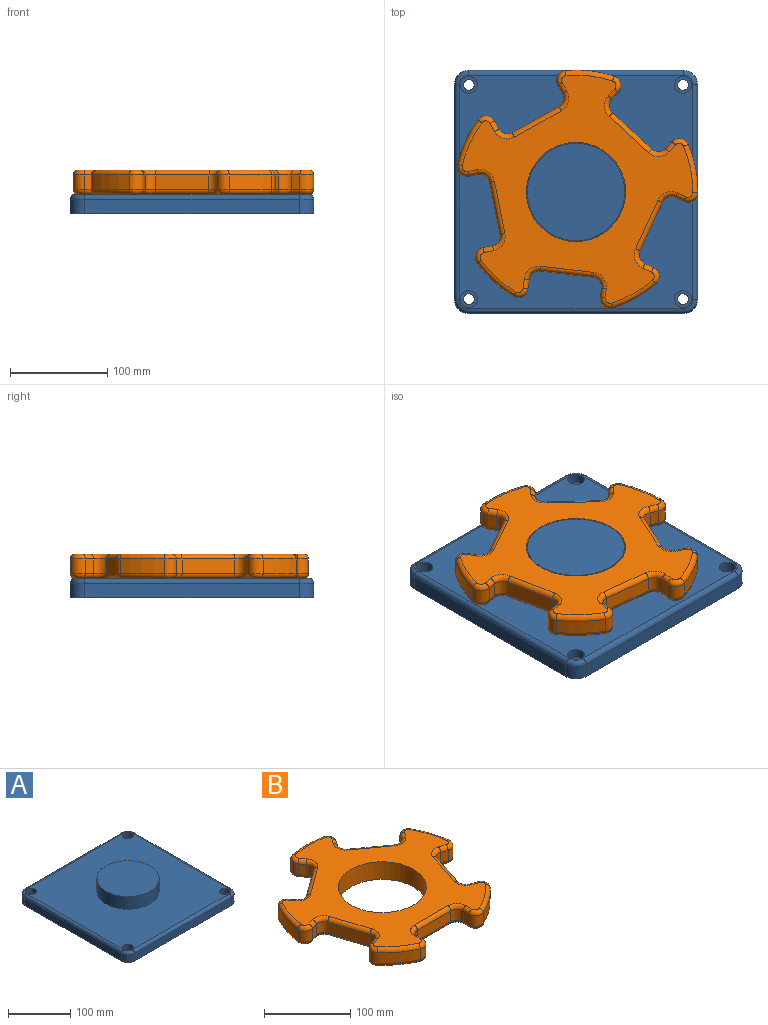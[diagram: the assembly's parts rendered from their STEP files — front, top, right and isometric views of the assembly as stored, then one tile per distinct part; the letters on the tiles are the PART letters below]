
ASSEMBLY  parts=2 mates=1
PART A: 32 faces, bbox 252.5x252.5x45 mm
  f0: plane 220x15mm, normal (1,0,0), area 3300mm2, adj f5,f8,f11,f27
  f1: plane 220x15mm, normal (0,1,0), area 3300mm2, adj f5,f8,f9,f31
  f2: plane 220x15mm, normal (-1,0,0), area 3300mm2, adj f5,f9,f10,f28
  f3: plane 220x15mm, normal (0,-1,0), area 3300mm2, adj f5,f10,f11,f24
  f4: plane 240x240mm, normal (0,0,1), area 48725.4mm2, adj f6,f14,f17,f20,f23,f24,f25,f26
  f5: plane 250x250mm, normal (0,0,-1), area 61926.7mm2, adj f0,f1,f2,f3,f8,f9,f10,f11
  f6: cylinder r=50mm len=100mm, axis (0,0,-1), area 7854mm2, adj f4,f7
  f7: plane 100x100mm, normal (0,0,1), area 7854mm2, adj f6
  f8: cylinder r=15mm len=15mm, axis (0,0,-1), area 353.4mm2, adj f0,f1,f5,f29
  f9: cylinder r=15mm len=15mm, axis (0,0,1), area 353.4mm2, adj f1,f2,f5,f30
  f10: cylinder r=15mm len=15mm, axis (0,0,-1), area 353.4mm2, adj f2,f3,f5,f26
  f11: cylinder r=15mm len=15mm, axis (0,0,1), area 353.4mm2, adj f0,f3,f5,f25
  f12: cylinder r=5.5mm len=11mm, axis (0,0,1), area 345.6mm2, adj f5,f13
  f13: plane 17.25x17.25mm, normal (0,0,1), area 138.7mm2, adj f12,f14
  f14: cylinder r=8.62mm len=17.25mm, axis (0,0,1), area 541.9mm2, adj f4,f13
  f15: cylinder r=5.5mm len=11mm, axis (0,0,1), area 345.6mm2, adj f5,f16
  f16: plane 17.25x17.25mm, normal (0,0,1), area 138.7mm2, adj f15,f17
  f17: cylinder r=8.62mm len=17.25mm, axis (0,0,1), area 541.9mm2, adj f4,f16
  f18: cylinder r=5.5mm len=11mm, axis (0,0,1), area 345.6mm2, adj f5,f19
  f19: plane 17.25x17.25mm, normal (0,0,1), area 138.7mm2, adj f18,f20
  f20: cylinder r=8.62mm len=17.25mm, axis (0,0,1), area 541.9mm2, adj f4,f19
  f21: cylinder r=5.5mm len=11mm, axis (0,0,1), area 345.6mm2, adj f5,f22
  f22: plane 17.25x17.25mm, normal (0,0,1), area 138.7mm2, adj f21,f23
  f23: cylinder r=8.62mm len=17.25mm, axis (0,0,1), area 541.9mm2, adj f4,f22
  f24: cylinder r=5mm len=220mm, axis (-1,0,0), area 1727.9mm2, adj f3,f4,f25,f26
  f25: torus R=10mm, axis (0,0,1), area 162.6mm2, adj f4,f11,f24,f27
  f26: torus R=10mm, axis (0,0,1), area 162.6mm2, adj f4,f10,f24,f28
  f27: cylinder r=5mm len=220mm, axis (0,-1,0), area 1727.9mm2, adj f0,f4,f25,f29
  f28: cylinder r=5mm len=220mm, axis (0,1,0), area 1727.9mm2, adj f2,f4,f26,f30
  f29: torus R=10mm, axis (0,0,1), area 162.6mm2, adj f4,f8,f27,f31
  f30: torus R=10mm, axis (0,0,1), area 162.6mm2, adj f4,f9,f28,f31
  f31: cylinder r=5mm len=220mm, axis (1,0,0), area 1727.9mm2, adj f1,f4,f29,f30
PART B: 123 faces, bbox 268.9x258.5x25 mm
  f0: plane 238.57x229.73mm, normal (0,0,1), area 21505.7mm2, adj f6,f83,f84,f85,f86,f87,f88,f89
  f1: plane 238.57x229.73mm, normal (0,0,-1), area 21505.7mm2, adj f6,f43,f44,f45,f46,f47,f48,f49
  f2: cylinder r=125mm len=47.82mm, axis (0,0,-1), area 759.5mm2, adj f34,f42,f74,f114
  f3: cylinder r=125mm len=50.29mm, axis (0,0,-1), area 759.5mm2, adj f27,f35,f75,f115
  f4: cylinder r=125mm len=47.82mm, axis (0,0,-1), area 759.5mm2, adj f20,f28,f59,f99
  f5: cylinder r=125mm len=40.68mm, axis (0,0,-1), area 759.5mm2, adj f13,f21,f43,f83
  f6: cylinder r=51mm len=102mm, axis (0,0,-1), area 8011.1mm2, adj f0,f1
  f7: cylinder r=125mm len=40.68mm, axis (0,0,-1), area 759.5mm2, adj f14,f41,f58,f98
  f8: plane 15x9.73mm, normal (-1,0,0), area 146mm2, adj f11,f14,f54,f94
  f9: plane 55x15mm, normal (0,-1,0), area 825mm2, adj f11,f12,f50,f90
  f10: plane 15x9.73mm, normal (1,0,0), area 146mm2, adj f12,f13,f46,f86
  f11: cylinder r=10mm len=15mm, axis (0,0,-1), area 235.6mm2, adj f8,f9,f52,f92
  f12: cylinder r=10mm len=15mm, axis (0,0,-1), area 235.6mm2, adj f9,f10,f48,f88
  f13: cylinder r=10mm len=15mm, axis (0,0,-1), area 299.5mm2, adj f5,f10,f44,f84
  f14: cylinder r=10mm len=15mm, axis (0,0,-1), area 299.5mm2, adj f7,f8,f56,f96
  f15: plane 15x9.26mm, normal (-0.31,0.95,0), area 146mm2, adj f18,f21,f47,f87
  f16: plane 52.31x17mm, normal (-0.95,-0.31,0), area 825mm2, adj f18,f19,f51,f91
  f17: plane 15x9.26mm, normal (0.31,-0.95,0), area 146mm2, adj f19,f20,f55,f95
  f18: cylinder r=10mm len=15mm, axis (0,0,-1), area 235.6mm2, adj f15,f16,f49,f89
  f19: cylinder r=10mm len=15mm, axis (0,0,-1), area 235.6mm2, adj f16,f17,f53,f93
  f20: cylinder r=10mm len=15mm, axis (0,0,-1), area 299.5mm2, adj f4,f17,f57,f97
  f21: cylinder r=10mm len=16.25mm, axis (0,0,-1), area 299.5mm2, adj f5,f15,f45,f85
  f22: plane 15x7.87mm, normal (0.81,0.59,0), area 146mm2, adj f25,f28,f63,f103
  f23: plane 44.5x32.33mm, normal (-0.59,0.81,0), area 825mm2, adj f25,f26,f67,f107
  f24: plane 15x7.87mm, normal (-0.81,-0.59,0), area 146mm2, adj f26,f27,f71,f111
  f25: cylinder r=10mm len=15mm, axis (0,0,-1), area 235.6mm2, adj f22,f23,f65,f105
  f26: cylinder r=10mm len=15mm, axis (0,0,-1), area 235.6mm2, adj f23,f24,f69,f109
  f27: cylinder r=10mm len=15.67mm, axis (0,0,-1), area 299.5mm2, adj f3,f24,f73,f113
  f28: cylinder r=10mm len=16.78mm, axis (0,0,-1), area 299.5mm2, adj f4,f22,f61,f101
  f29: plane 15x7.87mm, normal (0.81,-0.59,0), area 146mm2, adj f32,f35,f79,f119
  f30: plane 44.5x32.33mm, normal (0.59,0.81,0), area 825mm2, adj f32,f33,f82,f122
  f31: plane 15x7.87mm, normal (-0.81,0.59,0), area 146mm2, adj f33,f34,f78,f118
  f32: cylinder r=10mm len=15mm, axis (0,0,-1), area 235.6mm2, adj f29,f30,f81,f121
  f33: cylinder r=10mm len=15mm, axis (0,0,-1), area 235.6mm2, adj f30,f31,f80,f120
  f34: cylinder r=10mm len=16.78mm, axis (0,0,-1), area 299.5mm2, adj f2,f31,f76,f116
  f35: cylinder r=10mm len=15.67mm, axis (0,0,-1), area 299.5mm2, adj f3,f29,f77,f117
  f36: plane 15x9.26mm, normal (-0.31,-0.95,0), area 146mm2, adj f39,f42,f70,f110
  f37: plane 52.31x17mm, normal (0.95,-0.31,0), area 825mm2, adj f39,f40,f66,f106
  f38: plane 15x9.26mm, normal (0.31,0.95,0), area 146mm2, adj f40,f41,f62,f102
  f39: cylinder r=10mm len=15mm, axis (0,0,-1), area 235.6mm2, adj f36,f37,f68,f108
  f40: cylinder r=10mm len=15mm, axis (0,0,-1), area 235.6mm2, adj f37,f38,f64,f104
  f41: cylinder r=10mm len=16.25mm, axis (0,0,-1), area 299.5mm2, adj f7,f38,f60,f100
  f42: cylinder r=10mm len=15mm, axis (0,0,-1), area 299.5mm2, adj f2,f36,f72,f112
  f43: torus R=120mm, axis (0,0,1), area 391.9mm2, adj f1,f5,f44,f45
  f44: torus R=5mm, axis (0,0,1), area 128.3mm2, adj f1,f13,f43,f46
  f45: torus R=5mm, axis (0,0,1), area 128.3mm2, adj f1,f21,f43,f47
  f46: cylinder r=5mm len=9.73mm, axis (0,-1,0), area 76.4mm2, adj f1,f10,f44,f48
  f47: cylinder r=5mm len=10.8mm, axis (0.95,0.31,0), area 76.4mm2, adj f1,f15,f45,f49
  f48: torus R=15mm, axis (0,0,1), area 145.8mm2, adj f1,f12,f46,f50
  f49: torus R=15mm, axis (0,0,1), area 145.8mm2, adj f1,f18,f47,f51
  f50: cylinder r=5mm len=55mm, axis (-1,0,0), area 432mm2, adj f1,f9,f48,f52
  f51: cylinder r=5mm len=53.85mm, axis (-0.31,0.95,0), area 432mm2, adj f1,f16,f49,f53
  f52: torus R=15mm, axis (0,0,1), area 145.8mm2, adj f1,f11,f50,f54
  f53: torus R=15mm, axis (0,0,1), area 145.8mm2, adj f1,f19,f51,f55
  f54: cylinder r=5mm len=9.73mm, axis (0,1,0), area 76.4mm2, adj f1,f8,f52,f56
  f55: cylinder r=5mm len=10.8mm, axis (-0.95,-0.31,0), area 76.4mm2, adj f1,f17,f53,f57
  f56: torus R=5mm, axis (0,0,1), area 128.3mm2, adj f1,f14,f54,f58
  f57: torus R=5mm, axis (0,0,1), area 128.3mm2, adj f1,f20,f55,f59
  f58: torus R=120mm, axis (0,0,1), area 391.9mm2, adj f1,f7,f56,f60
  f59: torus R=120mm, axis (0,0,1), area 391.9mm2, adj f1,f4,f57,f61
  f60: torus R=5mm, axis (0,0,1), area 128.3mm2, adj f1,f41,f58,f62
  f61: torus R=5mm, axis (0,0,1), area 128.3mm2, adj f1,f28,f59,f63
  f62: cylinder r=5mm len=10.8mm, axis (0.95,-0.31,0), area 76.4mm2, adj f1,f38,f60,f64
  f63: cylinder r=5mm len=10.81mm, axis (0.59,-0.81,0), area 76.4mm2, adj f1,f22,f61,f65
  f64: torus R=15mm, axis (0,0,1), area 145.8mm2, adj f1,f40,f62,f66
  f65: torus R=15mm, axis (0,0,1), area 145.8mm2, adj f1,f25,f63,f67
  f66: cylinder r=5mm len=53.85mm, axis (-0.31,-0.95,0), area 432mm2, adj f1,f37,f64,f68
  f67: cylinder r=5mm len=47.44mm, axis (0.81,0.59,0), area 432mm2, adj f1,f23,f65,f69
  f68: torus R=15mm, axis (0,0,1), area 145.8mm2, adj f1,f39,f66,f70
  f69: torus R=15mm, axis (0,0,1), area 145.8mm2, adj f1,f26,f67,f71
  f70: cylinder r=5mm len=10.8mm, axis (-0.95,0.31,0), area 76.4mm2, adj f1,f36,f68,f72
  f71: cylinder r=5mm len=10.81mm, axis (-0.59,0.81,0), area 76.4mm2, adj f1,f24,f69,f73
  f72: torus R=5mm, axis (0,0,1), area 128.3mm2, adj f1,f42,f70,f74
  f73: torus R=5mm, axis (0,0,1), area 128.3mm2, adj f1,f27,f71,f75
  f74: torus R=120mm, axis (0,0,1), area 391.9mm2, adj f1,f2,f72,f76
  f75: torus R=120mm, axis (0,0,1), area 391.9mm2, adj f1,f3,f73,f77
  f76: torus R=5mm, axis (0,0,1), area 128.3mm2, adj f1,f34,f74,f78
  f77: torus R=5mm, axis (0,0,1), area 128.3mm2, adj f1,f35,f75,f79
  f78: cylinder r=5mm len=10.81mm, axis (0.59,0.81,0), area 76.4mm2, adj f1,f31,f76,f80
  f79: cylinder r=5mm len=10.81mm, axis (-0.59,-0.81,0), area 76.4mm2, adj f1,f29,f77,f81
  f80: torus R=15mm, axis (0,0,1), area 145.8mm2, adj f1,f33,f78,f82
  f81: torus R=15mm, axis (0,0,1), area 145.8mm2, adj f1,f32,f79,f82
  f82: cylinder r=5mm len=47.44mm, axis (0.81,-0.59,0), area 432mm2, adj f1,f30,f80,f81
  f83: torus R=120mm, axis (0,0,1), area 391.9mm2, adj f0,f5,f84,f85
  f84: torus R=5mm, axis (0,0,1), area 128.3mm2, adj f0,f13,f83,f86
  f85: torus R=5mm, axis (0,0,1), area 128.3mm2, adj f0,f21,f83,f87
  f86: cylinder r=5mm len=9.73mm, axis (0,1,0), area 76.4mm2, adj f0,f10,f84,f88
  f87: cylinder r=5mm len=10.8mm, axis (-0.95,-0.31,0), area 76.4mm2, adj f0,f15,f85,f89
  f88: torus R=15mm, axis (0,0,1), area 145.8mm2, adj f0,f12,f86,f90
  f89: torus R=15mm, axis (0,0,1), area 145.8mm2, adj f0,f18,f87,f91
  f90: cylinder r=5mm len=55mm, axis (1,0,0), area 432mm2, adj f0,f9,f88,f92
  f91: cylinder r=5mm len=53.85mm, axis (0.31,-0.95,0), area 432mm2, adj f0,f16,f89,f93
  f92: torus R=15mm, axis (0,0,1), area 145.8mm2, adj f0,f11,f90,f94
  f93: torus R=15mm, axis (0,0,1), area 145.8mm2, adj f0,f19,f91,f95
  f94: cylinder r=5mm len=9.73mm, axis (0,-1,0), area 76.4mm2, adj f0,f8,f92,f96
  f95: cylinder r=5mm len=10.8mm, axis (0.95,0.31,0), area 76.4mm2, adj f0,f17,f93,f97
  f96: torus R=5mm, axis (0,0,1), area 128.3mm2, adj f0,f14,f94,f98
  f97: torus R=5mm, axis (0,0,1), area 128.3mm2, adj f0,f20,f95,f99
  f98: torus R=120mm, axis (0,0,1), area 391.9mm2, adj f0,f7,f96,f100
  f99: torus R=120mm, axis (0,0,1), area 391.9mm2, adj f0,f4,f97,f101
  f100: torus R=5mm, axis (0,0,1), area 128.3mm2, adj f0,f41,f98,f102
  f101: torus R=5mm, axis (0,0,1), area 128.3mm2, adj f0,f28,f99,f103
  f102: cylinder r=5mm len=10.8mm, axis (-0.95,0.31,0), area 76.4mm2, adj f0,f38,f100,f104
  f103: cylinder r=5mm len=10.81mm, axis (-0.59,0.81,0), area 76.4mm2, adj f0,f22,f101,f105
  f104: torus R=15mm, axis (0,0,1), area 145.8mm2, adj f0,f40,f102,f106
  f105: torus R=15mm, axis (0,0,1), area 145.8mm2, adj f0,f25,f103,f107
  f106: cylinder r=5mm len=53.85mm, axis (0.31,0.95,0), area 432mm2, adj f0,f37,f104,f108
  f107: cylinder r=5mm len=47.44mm, axis (-0.81,-0.59,0), area 432mm2, adj f0,f23,f105,f109
  f108: torus R=15mm, axis (0,0,1), area 145.8mm2, adj f0,f39,f106,f110
  f109: torus R=15mm, axis (0,0,1), area 145.8mm2, adj f0,f26,f107,f111
  f110: cylinder r=5mm len=10.8mm, axis (0.95,-0.31,0), area 76.4mm2, adj f0,f36,f108,f112
  f111: cylinder r=5mm len=10.81mm, axis (0.59,-0.81,0), area 76.4mm2, adj f0,f24,f109,f113
  f112: torus R=5mm, axis (0,0,1), area 128.3mm2, adj f0,f42,f110,f114
  f113: torus R=5mm, axis (0,0,1), area 128.3mm2, adj f0,f27,f111,f115
  f114: torus R=120mm, axis (0,0,1), area 391.9mm2, adj f0,f2,f112,f116
  f115: torus R=120mm, axis (0,0,1), area 391.9mm2, adj f0,f3,f113,f117
  f116: torus R=5mm, axis (0,0,1), area 128.3mm2, adj f0,f34,f114,f118
  f117: torus R=5mm, axis (0,0,1), area 128.3mm2, adj f0,f35,f115,f119
  f118: cylinder r=5mm len=10.81mm, axis (-0.59,-0.81,0), area 76.4mm2, adj f0,f31,f116,f120
  f119: cylinder r=5mm len=10.81mm, axis (0.59,0.81,0), area 76.4mm2, adj f0,f29,f117,f121
  f120: torus R=15mm, axis (0,0,1), area 145.8mm2, adj f0,f33,f118,f122
  f121: torus R=15mm, axis (0,0,1), area 145.8mm2, adj f0,f32,f119,f122
  f122: cylinder r=5mm len=47.44mm, axis (-0.81,0.59,0), area 432mm2, adj f0,f30,f120,f121
PLACE A at identity fixed
PLACE B rot(axis=(0,0,-1),6.7deg) t=(0,0,0)mm
MATE revolute A.f6 <-> B.f2  axis (0,0,1) through (0,0,45)mm
